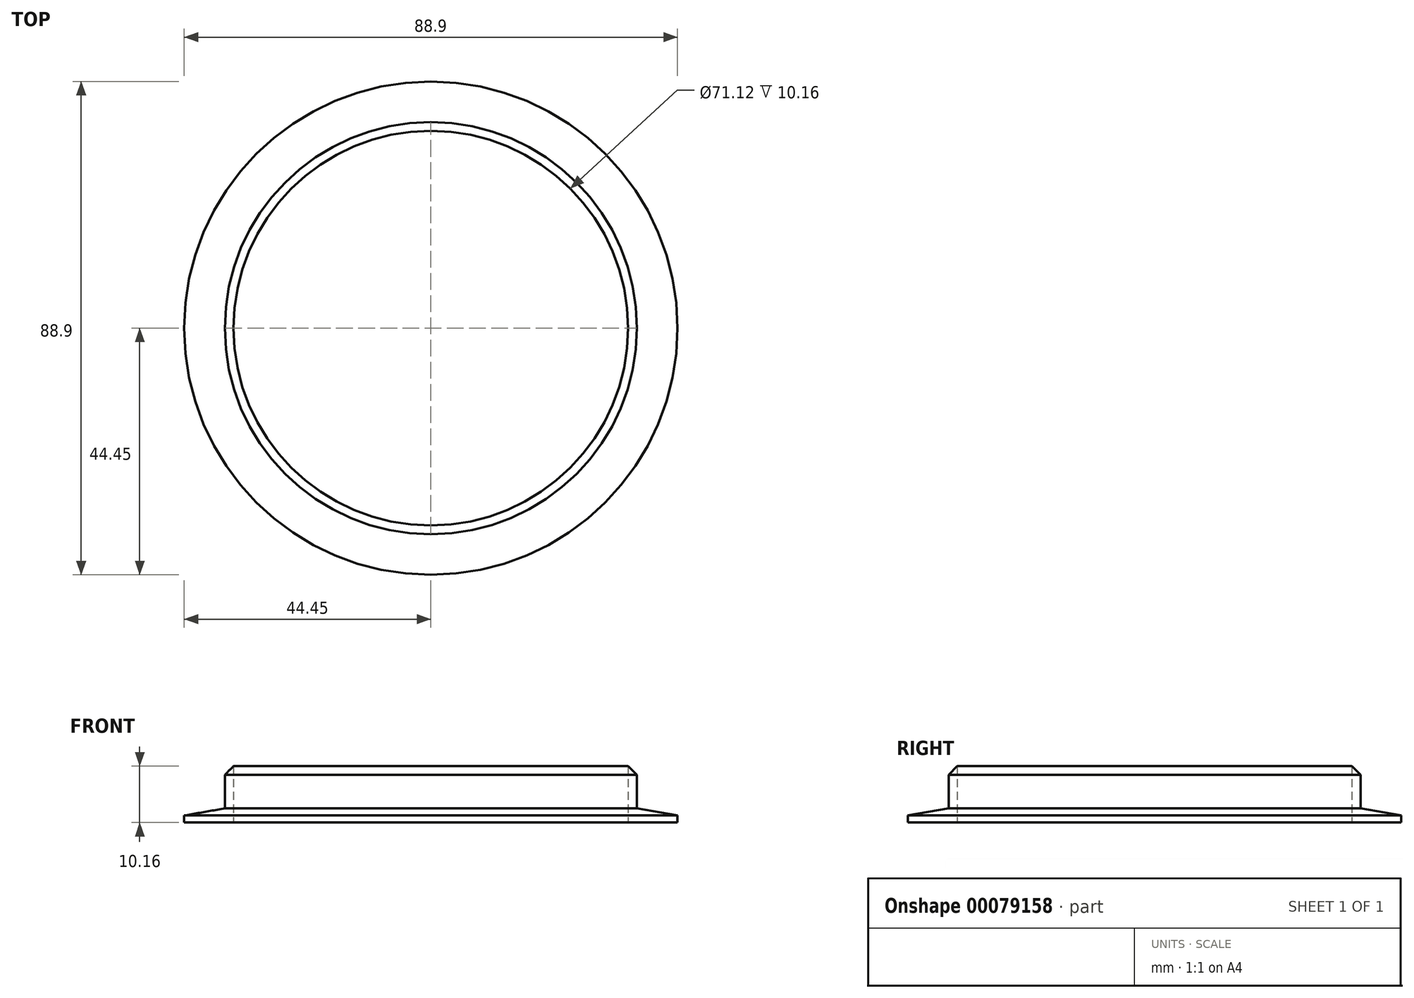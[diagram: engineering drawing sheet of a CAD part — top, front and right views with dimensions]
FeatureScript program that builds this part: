
annotation { "Feature Type Name" : "Feature", "Feature Type Description" : "" }
export const myFeature = defineFeature(function(context is Context, id is Id, definition is map)
    precondition{}
    {
        {
            var Q0;
            Q0=qCreatedBy(makeId("Front.planeOp"),FACE);
            var sketch = newSketch(context, id + "F0", { "sketchPlane" : qUnion([Q0])});
            skLineSegment(sketch, "E0", {"start": v(35.56, 0) * mm, "end": v(35.56, 10.16) * mm});
            skLineSegment(sketch, "E1", {"start": v(35.56, 10.16) * mm, "end": v(37.13, 10.16) * mm});
            skLineSegment(sketch, "E2", {"start": v(37.13, 10.16) * mm, "end": v(37.13, 2.54) * mm});
            skLineSegment(sketch, "E3", {"start": v(37.13, 2.54) * mm, "end": v(44.45, 1.27) * mm});
            skLineSegment(sketch, "E4", {"start": v(44.45, 1.27) * mm, "end": v(44.45, 0) * mm});
            skLineSegment(sketch, "E5", {"start": v(44.45, 0) * mm, "end": v(35.56, 0) * mm});
            skLineSegment(sketch, "E6", {"start": v(0, 0) * mm, "end": v(0, 25.47) * mm, "construction": true});
            skSolve(sketch);
        }
        {
            var Q0;
            Q0 = qSketchRegion(id + "F0", true);
            var Q1;
            Q1=sQuery(id+"F0.wireOp",EDGE,"E6");
            revolve(context, id + "F1", {"entities" : qUnion([Q0]), "axis" : qUnion([Q1]), "revolveType" : RevolveType.FULL});
        }
        {
            var Q0;
            Q0=makeQuery(id+"F1.opRevolve","SWEPT_EDGE",EDGE,{"disambiguationData":[OSD([sQuery(id+"F0.wireOp",EDGE,"E1"),sQuery(id+"F0.wireOp",EDGE,"E2")])]});
            chamfer(context, id + "F2", {"entities" : qUnion([Q0]), "width" : 1.57 * mm, "tangentPropagation" : true});
        }
    });
